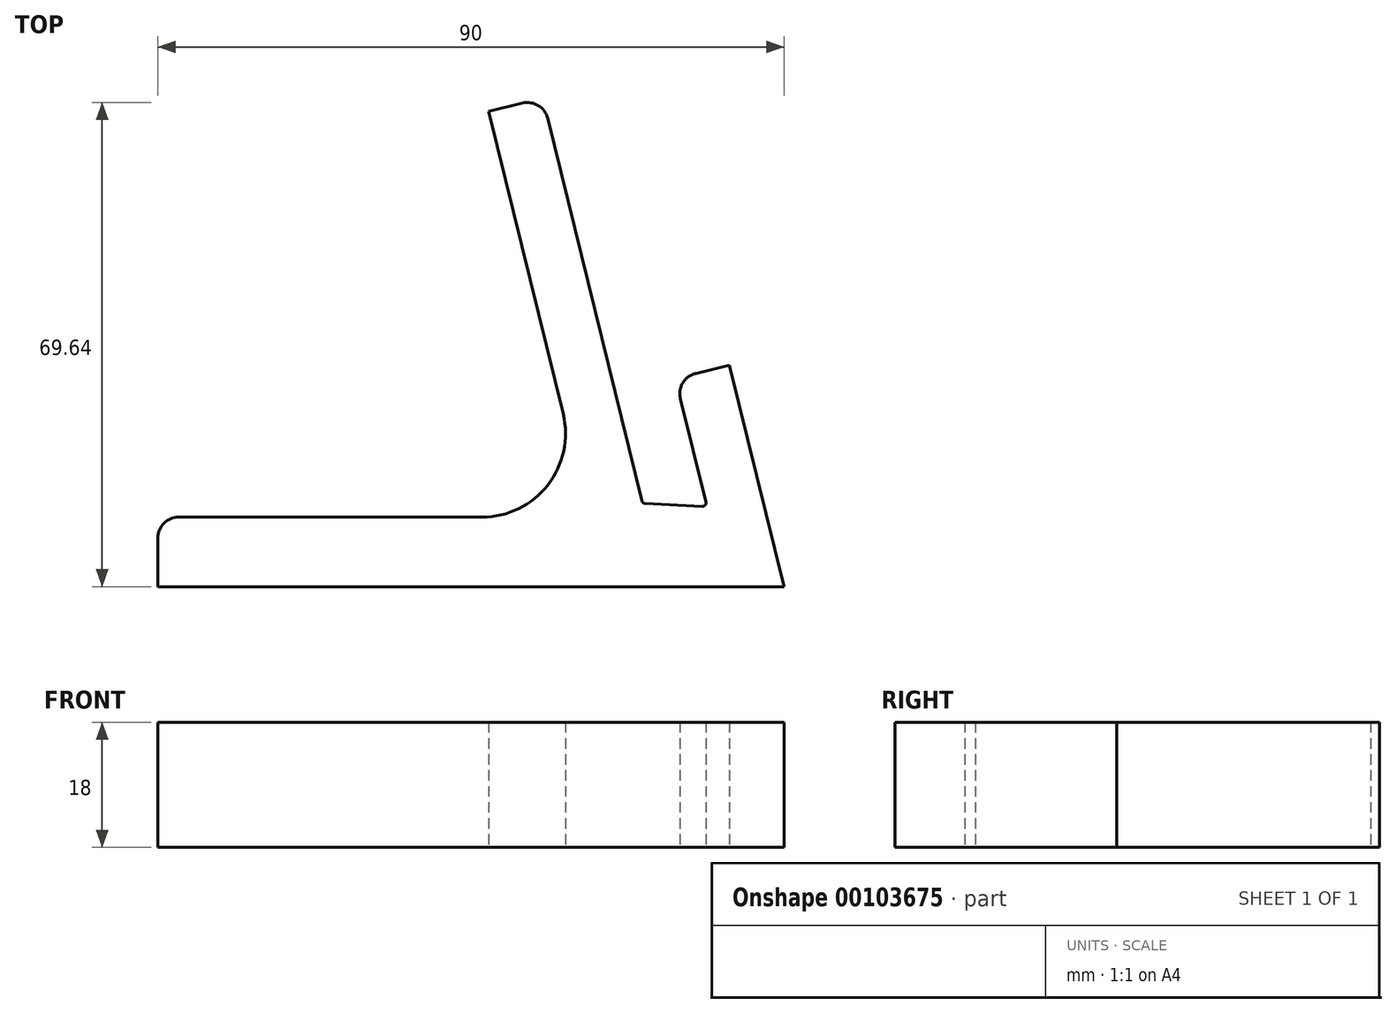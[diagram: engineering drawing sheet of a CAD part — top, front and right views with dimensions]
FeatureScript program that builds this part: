
annotation { "Feature Type Name" : "Feature", "Feature Type Description" : "" }
export const myFeature = defineFeature(function(context is Context, id is Id, definition is map)
    precondition{}
    {
        {
            var Q0;
            Q0=qCreatedBy(makeId("Top.planeOp"),FACE);
            var sketch = newSketch(context, id + "F0", { "sketchPlane" : qUnion([Q0])});
            skLineSegment(sketch, "E0.top", {"start": v(28.1, -15.61) * mm, "end": v(-61.9, -15.61) * mm});
            skLineSegment(sketch, "E0.right", {"start": v(-61.9, -5.61) * mm, "end": v(-61.9, -15.61) * mm});
            skLineSegment(sketch, "E1", {"start": v(28.1, -15.61) * mm, "end": v(20.27, 16.26) * mm});
            skLineSegment(sketch, "E2", {"start": v(20.27, 16.26) * mm, "end": v(12.5, 14.35) * mm});
            skLineSegment(sketch, "E3", {"start": v(12.5, 14.35) * mm, "end": v(17.03, -4.1) * mm});
            skLineSegment(sketch, "E4", {"start": v(7.75, -3.61) * mm, "end": v(-6.57, 54.66) * mm});
            skLineSegment(sketch, "E5", {"start": v(-6.57, 54.66) * mm, "end": v(-14.34, 52.75) * mm});
            skLineSegment(sketch, "E6.trimOffspring", {"start": v(0, -5.61) * mm, "end": v(-61.9, -5.61) * mm});
            skPoint(sketch, "E0.left.start.orphan", {"position": v(35, 4.6) * mm});
            skLineSegment(sketch, "E7", {"start": v(0, -5.61) * mm, "end": v(-14.34, 52.75) * mm});
            skLineSegment(sketch, "E8", {"start": v(7.75, -3.61) * mm, "end": v(17.03, -4.1) * mm});
            skSolve(sketch);
        }
        {
            var Q0;
            Q0=makeQuery(id+"F0.imprint","IMPRINT",FACE,{"disambiguationData":[TD([[makeQuery(id+"F0.imprint","IMPRINT",EDGE,{"derivedFrom":sQuery(id+"F0.wireOp",EDGE,"E0.top")}),-1.0]])]});
            extrude(context, id + "F1", {"entities" : qUnion([Q0]), "depth" : 18 * mm});
        }
        {
            var Q0;
            Q0=makeQuery(id+"F1.opExtrude","SWEPT_EDGE",EDGE,{"disambiguationData":[OSD([sQuery(id+"F0.wireOp",EDGE,"E2"),sQuery(id+"F0.wireOp",EDGE,"E3")])]});
            var Q1;
            Q1=makeQuery(id+"F1.opExtrude","SWEPT_EDGE",EDGE,{"disambiguationData":[OSD([sQuery(id+"F0.wireOp",EDGE,"E4"),sQuery(id+"F0.wireOp",EDGE,"E5")])]});
            fillet(context, id + "F2", {"entities" : qUnion([Q0, Q1]), "radius" : 3 * mm, "tangentPropagation" : true, "allowEdgeOverflow" : false});
        }
        {
            var Q0;
            Q0=makeQuery(id+"F1.opExtrude","SWEPT_EDGE",EDGE,{"disambiguationData":[OSD([sQuery(id+"F0.wireOp",EDGE,"E0.right"),sQuery(id+"F0.wireOp",EDGE,"E6.trimOffspring")])]});
            fillet(context, id + "F3", {"entities" : qUnion([Q0]), "radius" : 3 * mm, "tangentPropagation" : true, "allowEdgeOverflow" : false});
        }
        {
            var Q0;
            Q0=makeQuery(id+"F1.opExtrude","SWEPT_EDGE",EDGE,{"disambiguationData":[OSD([sQuery(id+"F0.wireOp",EDGE,"E6.trimOffspring"),sQuery(id+"F0.wireOp",EDGE,"E7")])]});
            fillet(context, id + "F4", {"entities" : qUnion([Q0]), "radius" : 12 * mm, "tangentPropagation" : true, "allowEdgeOverflow" : false});
        }
        {
            var Q0;
            Q0=makeQuery(id+"F1.opExtrude","SWEPT_EDGE",EDGE,{"disambiguationData":[OSD([sQuery(id+"F0.wireOp",EDGE,"E3"),sQuery(id+"F0.wireOp",EDGE,"E8")])]});
            var Q1;
            Q1=makeQuery(id+"F1.opExtrude","SWEPT_EDGE",EDGE,{"disambiguationData":[OSD([sQuery(id+"F0.wireOp",EDGE,"E4"),sQuery(id+"F0.wireOp",EDGE,"E8")])]});
            fillet(context, id + "F5", {"entities" : qUnion([Q0, Q1]), "radius" : .5 * mm, "tangentPropagation" : true, "allowEdgeOverflow" : false});
        }
    });
